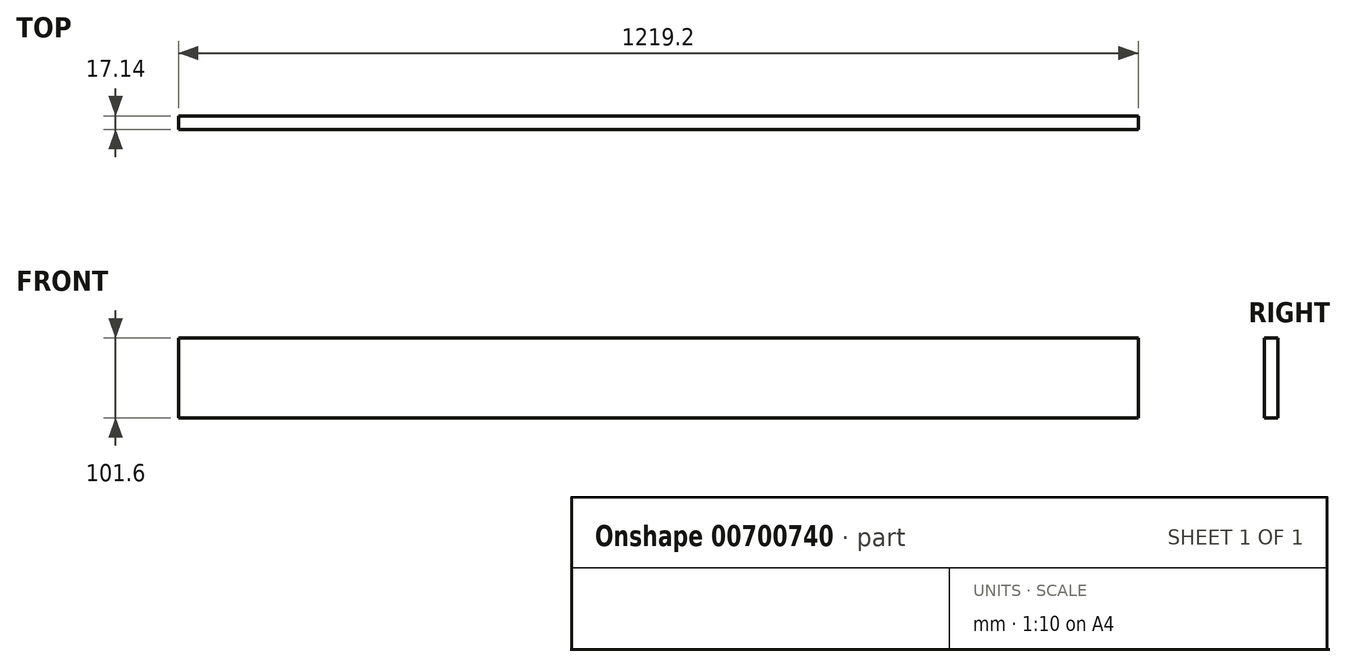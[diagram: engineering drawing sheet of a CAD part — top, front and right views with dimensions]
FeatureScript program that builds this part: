
annotation { "Feature Type Name" : "Feature", "Feature Type Description" : "" }
export const myFeature = defineFeature(function(context is Context, id is Id, definition is map)
    precondition{}
    {
        {
            var Q0;
            Q0=qCreatedBy(makeId("Front.planeOp"),FACE);
            var sketch = newSketch(context, id + "F0", { "sketchPlane" : qUnion([Q0])});
            skLineSegment(sketch, "E0.bottom", {"start": v(0, 0) * mm, "end": v(1219.2, 0) * mm});
            skLineSegment(sketch, "E0.top", {"start": v(0, 101.6) * mm, "end": v(1219.2, 101.6) * mm});
            skLineSegment(sketch, "E0.left", {"start": v(0, 0) * mm, "end": v(0, 101.6) * mm});
            skLineSegment(sketch, "E0.right", {"start": v(1219.2, 0) * mm, "end": v(1219.2, 101.6) * mm});
            skSolve(sketch);
        }
        {
            var Q0;
            Q0 = qSketchRegion(id + "F0", true);
            extrude(context, id + "F1", {"entities" : qUnion([Q0]), "depth" : 17.14 * mm, "offsetDistance" : 25.4 * mm});
        }
    });
